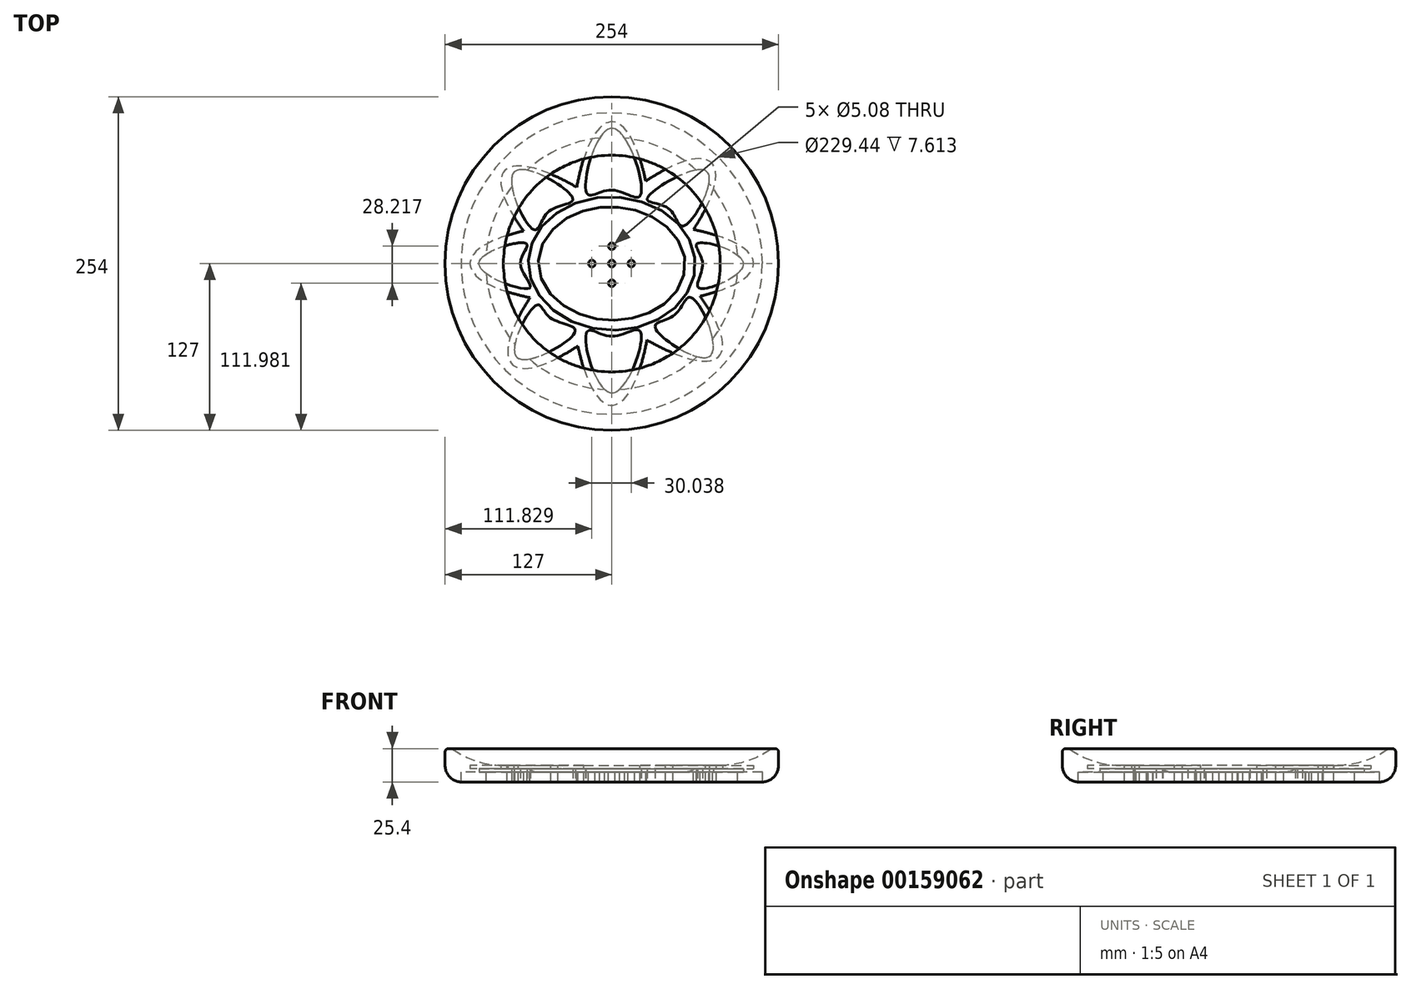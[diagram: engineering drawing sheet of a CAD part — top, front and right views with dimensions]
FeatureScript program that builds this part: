
annotation { "Feature Type Name" : "Feature", "Feature Type Description" : "" }
export const myFeature = defineFeature(function(context is Context, id is Id, definition is map)
    precondition{}
    {
        {
            var Q0;
            Q0=qCreatedBy(makeId("Top.planeOp"),FACE);
            var sketch = newSketch(context, id + "F0", { "sketchPlane" : qUnion([Q0])});
            skCircle(sketch, "E0", {"center": v(0, 0) * mm, "radius": 127 * mm});
            skSolve(sketch);
        }
        {
            var Q0;
            Q0 = qSketchRegion(id + "F0", true);
            extrude(context, id + "F1", {"entities" : qUnion([Q0]), "depth" : 25.4 * mm});
        }
        {
            var Q0;
            Q0=makeQuery(id+"F1.opExtrude","CAP_FACE",FACE,{"disambiguationData":[OSD([sQuery(id+"F0.wireOp",EDGE,"E0")])],"isStart":true});
            fillet(context, id + "F2", {"entities" : qUnion([Q0]), "radius" : 12.7 * mm, "tangentPropagation" : true, "allowEdgeOverflow" : false});
        }
        {
            var Q0;
            Q0=makeQuery(id+"F1.opExtrude","CAP_FACE",FACE,{"disambiguationData":[OSD([sQuery(id+"F0.wireOp",EDGE,"E0")])],"isStart":false});
            var sketch = newSketch(context, id + "F3", { "sketchPlane" : qUnion([Q0])});
            skCircle(sketch, "E1", {"center": v(0, 0) * mm, "radius": 121.92 * mm});
            skSolve(sketch);
        }
        {
            var Q0;
            Q0 = qSketchRegion(id + "F3", true);
            extrude(context, id + "F4", {"entities" : qUnion([Q0]), "operationType" : NewBodyOperationType.REMOVE, "oppositeDirection" : true, "depth" : 12.7 * mm});
        }
        {
            var Q0;
            Q0=makeQuery(id+"F4.boolean.opBoolean","COPY",FACE,{"derivedFrom":makeQuery(id+"F4.opExtrude","CAP_FACE",FACE,{"disambiguationData":[OSD([sQuery(id+"F3.wireOp",EDGE,"E1")])],"isStart":false})});
            var sketch = newSketch(context, id + "F5", { "sketchPlane" : qUnion([Q0])});
            skEllipse(sketch, "E2", {"center": v(0, 0) * mm, "majorRadius": 107.95 * mm, "minorRadius": 31.75 * mm, "majorAxis": v(-1, 0)});
            skEllipse(sketch, "E3", {"center": v(0, 0) * mm, "majorRadius": 107.95 * mm, "minorRadius": 31.75 * mm, "majorAxis": v(0, 1)});
            skEllipse(sketch, "E4", {"center": v(0, 0) * mm, "majorRadius": 107.95 * mm, "minorRadius": 31.75 * mm, "majorAxis": v(-0.76, 0.65)});
            skEllipse(sketch, "E5", {"center": v(0, 0) * mm, "majorRadius": 107.95 * mm, "minorRadius": 31.75 * mm, "majorAxis": v(0.7, 0.71)});
            skSolve(sketch);
        }
        {
            var Q0;
            {var subQ1=sQuery(id+"F5.wireOp",EDGE,"E2");var subQ5=sQuery(id+"F5.wireOp",EDGE,"E3");var subQ12=makeQuery(id+"F5.imprint","INTERSECT",VERTEX,{"disambiguationData":[OD(0.0)],"derivedFrom":[subQ1,subQ5]});Q0=makeQuery(id+"FsPKNqM0pqtH3t1_1.boolean.opBoolean","SPLIT",FACE,{"disambiguationData":[TD([makeQuery(id+"FsPKNqM0pqtH3t1_1.opExtrude","SWEPT_FACE",FACE,{"disambiguationData":[OSD([subQ1]),TDD([makeQuery(id+"F5.imprint","IMPRINT",EDGE,{"disambiguationData":[TD([[subQ12,-1.0]])],"derivedFrom":subQ1})])]})])],"derivedFrom":makeQuery(id+"F4.boolean.opBoolean","COPY",FACE,{"derivedFrom":makeQuery(id+"F4.opExtrude","CAP_FACE",FACE,{"disambiguationData":[OSD([sQuery(id+"F3.wireOp",EDGE,"E1")])],"isStart":false})})});}
            fillet(context, id + "F6", {"entities" : qUnion([Q0]), "radius" : 67.45 * mm, "tangentPropagation" : true, "allowEdgeOverflow" : false});
        }
        {
            var Q0;
            Q0 = qSketchRegion(id + "F5", true);
            extrude(context, id + "F7", {"entities" : qUnion([Q0]), "operationType" : NewBodyOperationType.REMOVE, "oppositeDirection" : true, "depth" : 2.54 * mm});
        }
        {
            var Q0;
            {var subQ1=sQuery(id+"F5.wireOp",EDGE,"E2");var subQ7=sQuery(id+"F5.wireOp",EDGE,"E3");var subQ10=makeQuery(id+"F5.imprint","INTERSECT",VERTEX,{"disambiguationData":[OD(0.0)],"derivedFrom":[subQ1,subQ7]});Q0=makeQuery(id+"F7.boolean.opBoolean","SPLIT",FACE,{"disambiguationData":[TD([makeQuery(id+"F7.opExtrude","SWEPT_FACE",FACE,{"disambiguationData":[OSD([subQ1]),TDD([makeQuery(id+"F5.imprint","IMPRINT",EDGE,{"disambiguationData":[TD([[subQ10,-1.0]])],"derivedFrom":subQ1})])]})])],"derivedFrom":makeQuery(id+"F4.boolean.opBoolean","COPY",FACE,{"derivedFrom":makeQuery(id+"F4.opExtrude","CAP_FACE",FACE,{"disambiguationData":[OSD([sQuery(id+"F3.wireOp",EDGE,"E1")])],"isStart":false})})});}
            var sketch = newSketch(context, id + "F8", { "sketchPlane" : qUnion([Q0])});
            skEllipse(sketch, "E6", {"center": v(0, 0) * mm, "majorRadius": 63.5 * mm, "minorRadius": 50.8 * mm, "majorAxis": v(-1, 0.03)});
            skSolve(sketch);
        }
        {
            var Q0;
            Q0 = qSketchRegion(id + "F8", true);
            extrude(context, id + "F9", {"entities" : qUnion([Q0]), "operationType" : NewBodyOperationType.REMOVE, "oppositeDirection" : true, "depth" : 5.08 * mm});
        }
        {
            var Q0;
            Q0=makeQuery(id+"F9.boolean.opBoolean","COPY",FACE,{"derivedFrom":makeQuery(id+"F9.opExtrude","CAP_FACE",FACE,{"disambiguationData":[OSD([sQuery(id+"F8.wireOp",EDGE,"E6")])],"isStart":false})});
            fillet(context, id + "F10", {"entities" : qUnion([Q0]), "radius" : 12.7 * mm, "tangentPropagation" : true, "allowEdgeOverflow" : false});
        }
        {
            var Q0;
            Q0=makeQuery(id+"F9.boolean.opBoolean","COPY",FACE,{"derivedFrom":makeQuery(id+"F9.opExtrude","CAP_FACE",FACE,{"disambiguationData":[OSD([sQuery(id+"F8.wireOp",EDGE,"E6")])],"isStart":false})});
            var sketch = newSketch(context, id + "F11", { "sketchPlane" : qUnion([Q0])});
            skCircle(sketch, "E7", {"center": v(0, 0) * mm, "radius": 2.54 * mm});
            skCircle(sketch, "E8", {"center": v(14.87, 0) * mm, "radius": 2.54 * mm});
            skCircle(sketch, "E9", {"center": v(0, -15.02) * mm, "radius": 2.54 * mm});
            skCircle(sketch, "E10", {"center": v(-15.17, 0) * mm, "radius": 2.54 * mm});
            skCircle(sketch, "E11", {"center": v(0, 13.2) * mm, "radius": 2.54 * mm});
            skSolve(sketch);
        }
        {
            var Q0;
            Q0 = qSketchRegion(id + "F11", true);
            extrude(context, id + "F12", {"entities" : qUnion([Q0]), "operationType" : NewBodyOperationType.REMOVE, "oppositeDirection" : true, "depth" : 25.4 * mm});
        }
        {
            var Q0;
            Q0=makeQuery(id+"F7.boolean.opBoolean","COPY",FACE,{"derivedFrom":makeQuery(id+"F7.opExtrude","CAP_FACE",FACE,{"disambiguationData":[OSD([sQuery(id+"F5.wireOp",EDGE,"E2"),sQuery(id+"F5.wireOp",EDGE,"E3"),sQuery(id+"F5.wireOp",EDGE,"E4"),sQuery(id+"F5.wireOp",EDGE,"E5")])],"isStart":false})});
            var sketch = newSketch(context, id + "F13", { "sketchPlane" : qUnion([Q0])});
            skFitSpline(sketch, "E12", {"points": [v(-65.23, 15.32) * mm, v(-69.48, 0) * mm, v(-62.8, -18.66) * mm, v(-101.04, 0) * mm, v(-65.23, 15.32) * mm]});
            skPoint(sketch, "E13.2.internal.snap0", {"position": v(31.75, 0) * mm});
            skFitSpline(sketch, "E13", {"points": [v(69.18, 0) * mm, v(65.23, 15.32) * mm, v(100.13, 0) * mm, v(66.45, -18.66) * mm, v(69.18, 0) * mm]});
            skFitSpline(sketch, "E14", {"points": [v(0, -55.37) * mm, v(-19.12, -52.34) * mm, v(0, -98.46) * mm, v(21.85, -52.04) * mm, v(0, -55.37) * mm]});
            skFitSpline(sketch, "E15", {"points": [v(0, 55.98) * mm, v(21.85, 52.04) * mm, v(0, 103) * mm, v(-19.12, 53.86) * mm, v(0, 55.98) * mm]});
            skFitSpline(sketch, "E16", {"points": [v(-47.64, 39.9) * mm, v(-29.73, 49.6) * mm, v(-74.03, 69.94) * mm, v(-59.47, 25.94) * mm, v(-47.64, 39.9) * mm]});
            skPoint(sketch, "E17.2.internal.snap0", {"position": v(81.93, -70.29) * mm});
            skFitSpline(sketch, "E17", {"points": [v(47.94, -38.99) * mm, v(33.07, -48.7) * mm, v(74.94, -70.29) * mm, v(60.68, -25.94) * mm, v(47.94, -38.99) * mm]});
            skFitSpline(sketch, "E18", {"points": [v(43.08, 42.02) * mm, v(54.92, 28.67) * mm, v(72.52, 69.94) * mm, v(27, 49.6) * mm, v(43.08, 42.02) * mm]});
            skPoint(sketch, "E19.1.internal.snap0", {"position": v(0, -31.75) * mm});
            skFitSpline(sketch, "E19", {"points": [v(-47.03, -41.11) * mm, v(-57.35, -31.75) * mm, v(-72.21, -71.45) * mm, v(-27.91, -51.73) * mm, v(-47.03, -41.11) * mm]});
            skSolve(sketch);
        }
        {
            var Q0;
            Q0=makeQuery(id+"F1.opExtrude","CAP_FACE",FACE,{"disambiguationData":[OSD([sQuery(id+"F0.wireOp",EDGE,"E0")])],"isStart":false});
            fillet(context, id + "F14", {"entities" : qUnion([Q0]), "radius" : 2.54 * mm, "tangentPropagation" : true, "allowEdgeOverflow" : false});
        }
        {
            var Q0;
            Q0 = qSketchRegion(id + "F13", true);
            extrude(context, id + "F15", {"entities" : qUnion([Q0]), "operationType" : NewBodyOperationType.REMOVE, "oppositeDirection" : true, "depth" : 25.4 * mm});
        }
        {
            var Q0;
            {var subQ0=sQuery(id+"F3.wireOp",EDGE,"E1");var subQ1=sQuery(id+"F5.wireOp",EDGE,"E5");var subQ2=sQuery(id+"F5.wireOp",EDGE,"E2");var subQ3=makeQuery(id+"F5.imprint","INTERSECT",VERTEX,{"disambiguationData":[OD(0.0)],"derivedFrom":[subQ2,subQ1]});var subQ4=sQuery(id+"F5.wireOp",EDGE,"E4");var subQ5=sQuery(id+"F5.wireOp",EDGE,"E3");Q0=makeQuery(id+"F7.boolean.opBoolean","SPLIT",FACE,{"disambiguationData":[TD([makeQuery(id+"F6.opFillet","BLEND_FACE",FACE,{"disambiguationData":[OSD([subQ0])]}),makeQuery(id+"F7.opExtrude","CAP_FACE",FACE,{"disambiguationData":[OSD([subQ2,subQ5,subQ4,subQ1])],"isStart":true}),makeQuery(id+"F7.opExtrude","SWEPT_FACE",FACE,{"disambiguationData":[OSD([subQ2]),TDD([makeQuery(id+"F5.imprint","IMPRINT",EDGE,{"disambiguationData":[TD([[subQ3,1.0]])],"derivedFrom":subQ2})])]}),makeQuery(id+"F7.opExtrude","SWEPT_FACE",FACE,{"disambiguationData":[OSD([subQ1]),TDD([makeQuery(id+"F5.imprint","IMPRINT",EDGE,{"disambiguationData":[TD([[subQ3,-1.0]])],"derivedFrom":subQ1})])]})])],"derivedFrom":makeQuery(id+"F4.boolean.opBoolean","COPY",FACE,{"derivedFrom":makeQuery(id+"F4.opExtrude","CAP_FACE",FACE,{"disambiguationData":[OSD([subQ0])],"isStart":false})})});}
            var Q1;
            {var subQ0=sQuery(id+"F3.wireOp",EDGE,"E1");var subQ1=sQuery(id+"F5.wireOp",EDGE,"E5");var subQ2=sQuery(id+"F5.wireOp",EDGE,"E4");var subQ3=sQuery(id+"F5.wireOp",EDGE,"E3");var subQ4=sQuery(id+"F5.wireOp",EDGE,"E2");var subQ5=makeQuery(id+"F5.imprint","INTERSECT",VERTEX,{"disambiguationData":[OD(1.0)],"derivedFrom":[subQ3,subQ1]});Q1=makeQuery(id+"F7.boolean.opBoolean","SPLIT",FACE,{"disambiguationData":[TD([makeQuery(id+"F6.opFillet","BLEND_FACE",FACE,{"disambiguationData":[OSD([subQ0])]}),makeQuery(id+"F7.opExtrude","CAP_FACE",FACE,{"disambiguationData":[OSD([subQ4,subQ3,subQ2,subQ1])],"isStart":true}),makeQuery(id+"F7.opExtrude","SWEPT_FACE",FACE,{"disambiguationData":[OSD([subQ3]),TDD([makeQuery(id+"F5.imprint","IMPRINT",EDGE,{"disambiguationData":[TD([[subQ5,-1.0]])],"derivedFrom":subQ3})])]}),makeQuery(id+"F7.opExtrude","SWEPT_FACE",FACE,{"disambiguationData":[OSD([subQ1]),TDD([makeQuery(id+"F5.imprint","IMPRINT",EDGE,{"disambiguationData":[TD([[makeQuery(id+"F5.imprint","INTERSECT",VERTEX,{"disambiguationData":[OD(0.0)],"derivedFrom":[subQ4,subQ1]}),-1.0]])],"derivedFrom":subQ1})])]})])],"derivedFrom":makeQuery(id+"F4.boolean.opBoolean","COPY",FACE,{"derivedFrom":makeQuery(id+"F4.opExtrude","CAP_FACE",FACE,{"disambiguationData":[OSD([subQ0])],"isStart":false})})});}
            var Q2;
            {var subQ0=sQuery(id+"F3.wireOp",EDGE,"E1");var subQ1=sQuery(id+"F5.wireOp",EDGE,"E5");var subQ2=sQuery(id+"F5.wireOp",EDGE,"E4");var subQ3=sQuery(id+"F5.wireOp",EDGE,"E3");var subQ4=sQuery(id+"F5.wireOp",EDGE,"E2");Q2=makeQuery(id+"F7.boolean.opBoolean","SPLIT",FACE,{"disambiguationData":[TD([makeQuery(id+"F6.opFillet","BLEND_FACE",FACE,{"disambiguationData":[OSD([subQ0])]}),makeQuery(id+"F7.opExtrude","CAP_FACE",FACE,{"disambiguationData":[OSD([subQ4,subQ3,subQ2,subQ1])],"isStart":true}),makeQuery(id+"F7.opExtrude","SWEPT_FACE",FACE,{"disambiguationData":[OSD([subQ3]),TDD([makeQuery(id+"F5.imprint","IMPRINT",EDGE,{"disambiguationData":[TD([[makeQuery(id+"F5.imprint","INTERSECT",VERTEX,{"disambiguationData":[OD(1.0)],"derivedFrom":[subQ3,subQ1]}),-1.0]])],"derivedFrom":subQ3})])]}),makeQuery(id+"F7.opExtrude","SWEPT_FACE",FACE,{"disambiguationData":[OSD([subQ2]),TDD([makeQuery(id+"F5.imprint","IMPRINT",EDGE,{"disambiguationData":[TD([[makeQuery(id+"F5.imprint","INTERSECT",VERTEX,{"disambiguationData":[OD(1.0)],"derivedFrom":[subQ4,subQ2]}),1.0]])],"derivedFrom":subQ2})])]})])],"derivedFrom":makeQuery(id+"F4.boolean.opBoolean","COPY",FACE,{"derivedFrom":makeQuery(id+"F4.opExtrude","CAP_FACE",FACE,{"disambiguationData":[OSD([subQ0])],"isStart":false})})});}
            var Q3;
            {var subQ0=sQuery(id+"F3.wireOp",EDGE,"E1");var subQ1=sQuery(id+"F5.wireOp",EDGE,"E4");var subQ2=sQuery(id+"F5.wireOp",EDGE,"E2");var subQ3=makeQuery(id+"F5.imprint","INTERSECT",VERTEX,{"disambiguationData":[OD(1.0)],"derivedFrom":[subQ2,subQ1]});var subQ4=sQuery(id+"F5.wireOp",EDGE,"E5");var subQ5=sQuery(id+"F5.wireOp",EDGE,"E3");Q3=makeQuery(id+"F7.boolean.opBoolean","SPLIT",FACE,{"disambiguationData":[TD([makeQuery(id+"F6.opFillet","BLEND_FACE",FACE,{"disambiguationData":[OSD([subQ0])]}),makeQuery(id+"F7.opExtrude","CAP_FACE",FACE,{"disambiguationData":[OSD([subQ2,subQ5,subQ1,subQ4])],"isStart":true}),makeQuery(id+"F7.opExtrude","SWEPT_FACE",FACE,{"disambiguationData":[OSD([subQ2]),TDD([makeQuery(id+"F5.imprint","IMPRINT",EDGE,{"disambiguationData":[TD([[subQ3,-1.0]])],"derivedFrom":subQ2})])]}),makeQuery(id+"F7.opExtrude","SWEPT_FACE",FACE,{"disambiguationData":[OSD([subQ1]),TDD([makeQuery(id+"F5.imprint","IMPRINT",EDGE,{"disambiguationData":[TD([[subQ3,1.0]])],"derivedFrom":subQ1})])]})])],"derivedFrom":makeQuery(id+"F4.boolean.opBoolean","COPY",FACE,{"derivedFrom":makeQuery(id+"F4.opExtrude","CAP_FACE",FACE,{"disambiguationData":[OSD([subQ0])],"isStart":false})})});}
            var Q4;
            {var subQ0=sQuery(id+"F3.wireOp",EDGE,"E1");var subQ1=sQuery(id+"F5.wireOp",EDGE,"E4");var subQ2=sQuery(id+"F5.wireOp",EDGE,"E2");var subQ3=sQuery(id+"F5.wireOp",EDGE,"E5");var subQ4=makeQuery(id+"F5.imprint","INTERSECT",VERTEX,{"disambiguationData":[OD(2.0)],"derivedFrom":[subQ2,subQ3]});var subQ5=sQuery(id+"F5.wireOp",EDGE,"E3");Q4=makeQuery(id+"F7.boolean.opBoolean","SPLIT",FACE,{"disambiguationData":[TD([makeQuery(id+"F6.opFillet","BLEND_FACE",FACE,{"disambiguationData":[OSD([subQ0])]}),makeQuery(id+"F7.opExtrude","CAP_FACE",FACE,{"disambiguationData":[OSD([subQ2,subQ5,subQ1,subQ3])],"isStart":true}),makeQuery(id+"F7.opExtrude","SWEPT_FACE",FACE,{"disambiguationData":[OSD([subQ2]),TDD([makeQuery(id+"F5.imprint","IMPRINT",EDGE,{"disambiguationData":[TD([[makeQuery(id+"F5.imprint","INTERSECT",VERTEX,{"disambiguationData":[OD(1.0)],"derivedFrom":[subQ2,subQ1]}),-1.0]])],"derivedFrom":subQ2})])]}),makeQuery(id+"F7.opExtrude","SWEPT_FACE",FACE,{"disambiguationData":[OSD([subQ3]),TDD([makeQuery(id+"F5.imprint","IMPRINT",EDGE,{"disambiguationData":[TD([[subQ4,-1.0]])],"derivedFrom":subQ3})])]})])],"derivedFrom":makeQuery(id+"F4.boolean.opBoolean","COPY",FACE,{"derivedFrom":makeQuery(id+"F4.opExtrude","CAP_FACE",FACE,{"disambiguationData":[OSD([subQ0])],"isStart":false})})});}
            var Q5;
            {var subQ0=sQuery(id+"F3.wireOp",EDGE,"E1");var subQ1=sQuery(id+"F5.wireOp",EDGE,"E4");var subQ2=sQuery(id+"F5.wireOp",EDGE,"E3");var subQ3=sQuery(id+"F5.wireOp",EDGE,"E5");var subQ5=sQuery(id+"F5.wireOp",EDGE,"E2");Q5=makeQuery(id+"F7.boolean.opBoolean","SPLIT",FACE,{"disambiguationData":[TD([makeQuery(id+"F6.opFillet","BLEND_FACE",FACE,{"disambiguationData":[OSD([subQ0])]}),makeQuery(id+"F7.opExtrude","CAP_FACE",FACE,{"disambiguationData":[OSD([subQ5,subQ2,subQ1,subQ3])],"isStart":true}),makeQuery(id+"F7.opExtrude","SWEPT_FACE",FACE,{"disambiguationData":[OSD([subQ2]),TDD([makeQuery(id+"F5.imprint","IMPRINT",EDGE,{"disambiguationData":[TD([[makeQuery(id+"F5.imprint","INTERSECT",VERTEX,{"disambiguationData":[OD(0.0)],"derivedFrom":[subQ2,subQ1]}),1.0]])],"derivedFrom":subQ2})])]}),makeQuery(id+"F7.opExtrude","SWEPT_FACE",FACE,{"disambiguationData":[OSD([subQ3]),TDD([makeQuery(id+"F5.imprint","IMPRINT",EDGE,{"disambiguationData":[TD([[makeQuery(id+"F5.imprint","INTERSECT",VERTEX,{"disambiguationData":[OD(2.0)],"derivedFrom":[subQ5,subQ3]}),-1.0]])],"derivedFrom":subQ3})])]})])],"derivedFrom":makeQuery(id+"F4.boolean.opBoolean","COPY",FACE,{"derivedFrom":makeQuery(id+"F4.opExtrude","CAP_FACE",FACE,{"disambiguationData":[OSD([subQ0])],"isStart":false})})});}
            var Q6;
            {var subQ0=sQuery(id+"F3.wireOp",EDGE,"E1");var subQ1=sQuery(id+"F5.wireOp",EDGE,"E4");var subQ2=sQuery(id+"F5.wireOp",EDGE,"E3");var subQ3=makeQuery(id+"F5.imprint","INTERSECT",VERTEX,{"disambiguationData":[OD(0.0)],"derivedFrom":[subQ2,subQ1]});var subQ4=sQuery(id+"F5.wireOp",EDGE,"E5");var subQ5=sQuery(id+"F5.wireOp",EDGE,"E2");Q6=makeQuery(id+"F7.boolean.opBoolean","SPLIT",FACE,{"disambiguationData":[TD([makeQuery(id+"F6.opFillet","BLEND_FACE",FACE,{"disambiguationData":[OSD([subQ0])]}),makeQuery(id+"F7.opExtrude","CAP_FACE",FACE,{"disambiguationData":[OSD([subQ5,subQ2,subQ1,subQ4])],"isStart":true}),makeQuery(id+"F7.opExtrude","SWEPT_FACE",FACE,{"disambiguationData":[OSD([subQ2]),TDD([makeQuery(id+"F5.imprint","IMPRINT",EDGE,{"disambiguationData":[TD([[subQ3,1.0]])],"derivedFrom":subQ2})])]}),makeQuery(id+"F7.opExtrude","SWEPT_FACE",FACE,{"disambiguationData":[OSD([subQ1]),TDD([makeQuery(id+"F5.imprint","IMPRINT",EDGE,{"disambiguationData":[TD([[makeQuery(id+"F5.imprint","INTERSECT",VERTEX,{"disambiguationData":[OD(3.0)],"derivedFrom":[subQ5,subQ1]}),1.0]])],"derivedFrom":subQ1})])]})])],"derivedFrom":makeQuery(id+"F4.boolean.opBoolean","COPY",FACE,{"derivedFrom":makeQuery(id+"F4.opExtrude","CAP_FACE",FACE,{"disambiguationData":[OSD([subQ0])],"isStart":false})})});}
            var Q7;
            {var subQ0=sQuery(id+"F3.wireOp",EDGE,"E1");var subQ1=sQuery(id+"F5.wireOp",EDGE,"E5");var subQ2=sQuery(id+"F5.wireOp",EDGE,"E2");var subQ3=sQuery(id+"F5.wireOp",EDGE,"E4");var subQ4=makeQuery(id+"F5.imprint","INTERSECT",VERTEX,{"disambiguationData":[OD(3.0)],"derivedFrom":[subQ2,subQ3]});var subQ5=sQuery(id+"F5.wireOp",EDGE,"E3");Q7=makeQuery(id+"F7.boolean.opBoolean","SPLIT",FACE,{"disambiguationData":[TD([makeQuery(id+"F6.opFillet","BLEND_FACE",FACE,{"disambiguationData":[OSD([subQ0])]}),makeQuery(id+"F7.opExtrude","CAP_FACE",FACE,{"disambiguationData":[OSD([subQ2,subQ5,subQ3,subQ1])],"isStart":true}),makeQuery(id+"F7.opExtrude","SWEPT_FACE",FACE,{"disambiguationData":[OSD([subQ2]),TDD([makeQuery(id+"F5.imprint","IMPRINT",EDGE,{"disambiguationData":[TD([[makeQuery(id+"F5.imprint","INTERSECT",VERTEX,{"disambiguationData":[OD(0.0)],"derivedFrom":[subQ2,subQ1]}),1.0]])],"derivedFrom":subQ2})])]}),makeQuery(id+"F7.opExtrude","SWEPT_FACE",FACE,{"disambiguationData":[OSD([subQ3]),TDD([makeQuery(id+"F5.imprint","IMPRINT",EDGE,{"disambiguationData":[TD([[subQ4,1.0]])],"derivedFrom":subQ3})])]})])],"derivedFrom":makeQuery(id+"F4.boolean.opBoolean","COPY",FACE,{"derivedFrom":makeQuery(id+"F4.opExtrude","CAP_FACE",FACE,{"disambiguationData":[OSD([subQ0])],"isStart":false})})});}
            extrude(context, id + "F16", {"entities" : qUnion([Q0, Q1, Q2, Q3, Q4, Q5, Q6, Q7]), "operationType" : NewBodyOperationType.REMOVE, "oppositeDirection" : true, "depth" : 25.4 * mm});
        }
        {
            var Q0;
            Q0=makeQuery(id+"F9.boolean.opBoolean","COPY",FACE,{"derivedFrom":makeQuery(id+"F9.opExtrude","CAP_FACE",FACE,{"disambiguationData":[OSD([sQuery(id+"F8.wireOp",EDGE,"E6")])],"isStart":false})});
            var sketch = newSketch(context, id + "F17", { "sketchPlane" : qUnion([Q0])});
            skCircle(sketch, "E20", {"center": v(0, 0) * mm, "radius": 114.72 * mm});
            skCircle(sketch, "E21", {"center": v(0, 0) * mm, "radius": 96.03 * mm});
            skSolve(sketch);
        }
        {
            var Q0;
            Q0 = qSketchRegion(id + "F17", true);
            extrude(context, id + "F18", {"entities" : qUnion([Q0]), "operationType" : NewBodyOperationType.REMOVE, "oppositeDirection" : true, "depth" : 25.4 * mm});
        }
    });
